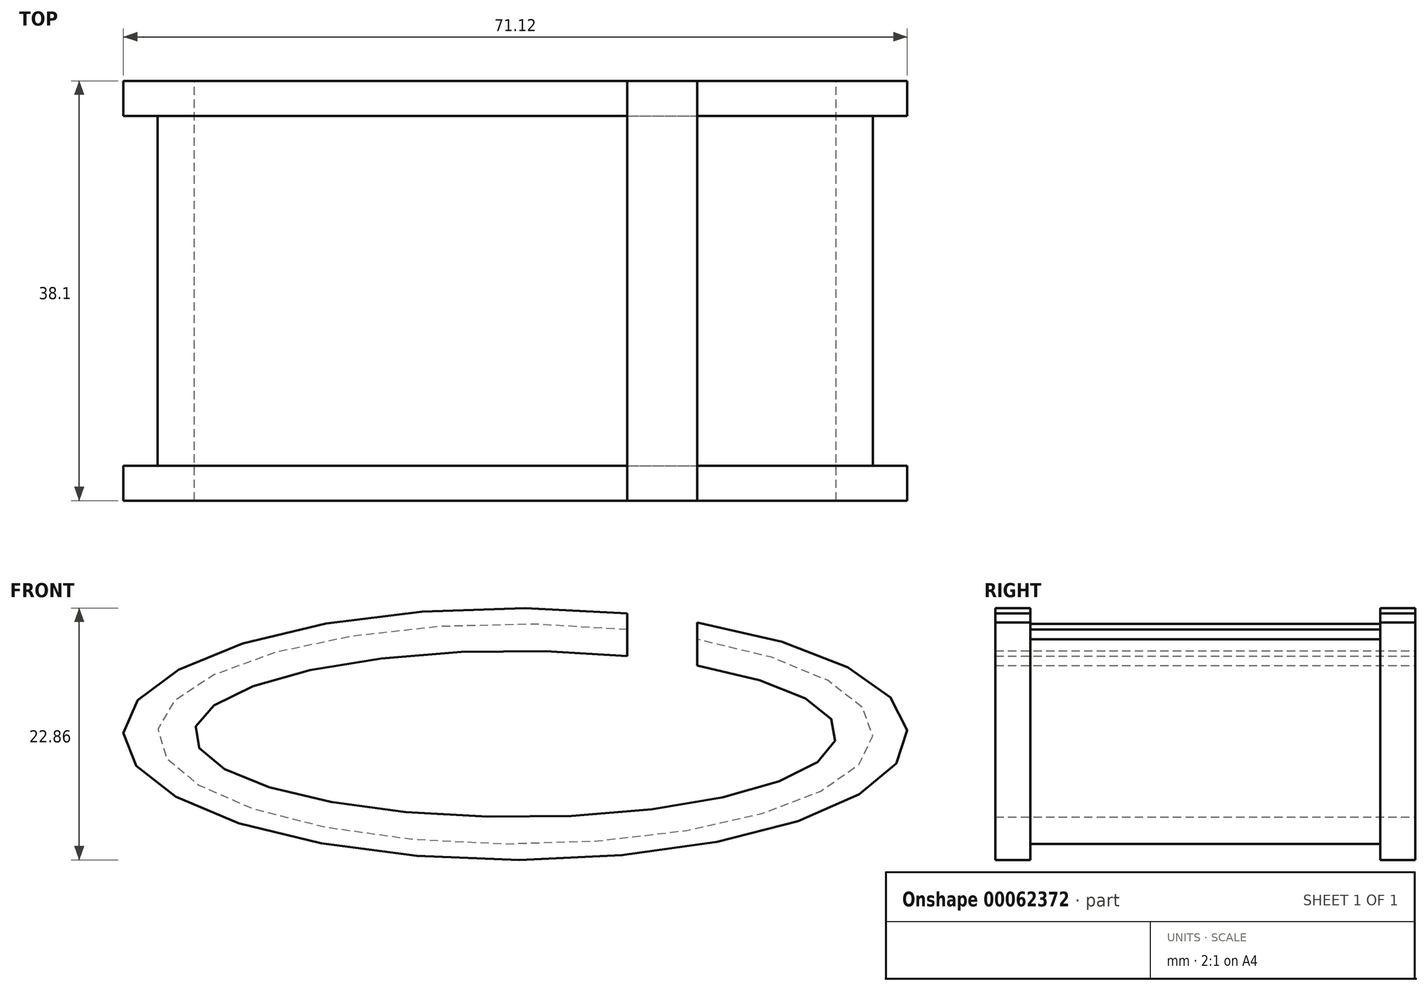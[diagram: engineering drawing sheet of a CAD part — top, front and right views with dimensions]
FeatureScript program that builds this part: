
annotation { "Feature Type Name" : "Feature", "Feature Type Description" : "" }
export const myFeature = defineFeature(function(context is Context, id is Id, definition is map)
    precondition{}
    {
        {
            var Q0;
            Q0=qCreatedBy(makeId("Front.planeOp"),FACE);
            var sketch = newSketch(context, id + "F0", { "sketchPlane" : qUnion([Q0])});
            skLineSegment(sketch, "E0", {"start": v(-32.45, 0) * mm, "end": v(32.45, 0) * mm, "construction": true});
            skLineSegment(sketch, "E1", {"start": v(0, 9.98) * mm, "end": v(0, -9.98) * mm, "construction": true});
            skPoint(sketch, "E2", {"position": v(0, 0) * mm});
            skEllipse(sketch, "E3", {"center": v(0, 0) * mm, "majorRadius": 9.98 * mm, "minorRadius": 32.45 * mm, "majorAxis": v(0, 1)});
            skSolve(sketch);
        }
        {
            var Q0;
            Q0=makeQuery(id+"F0.imprint","IMPRINT",FACE,{"disambiguationData":[TD([[makeQuery(id+"F0.imprint","IMPRINT",EDGE,{"derivedFrom":sQuery(id+"F0.wireOp",EDGE,"E3")}),1.0]])]});
            extrude(context, id + "F1", {"entities" : qUnion([Q0]), "depth" : 15.88 * mm});
        }
        {
            var Q0;
            Q0=makeQuery(id+"F1.opExtrude","CAP_FACE",FACE,{"disambiguationData":[OSD([sQuery(id+"F0.wireOp",EDGE,"E3")])],"isStart":false});
            var sketch = newSketch(context, id + "F2", { "sketchPlane" : qUnion([Q0])});
            skLineSegment(sketch, "E4", {"start": v(0, 0) * mm, "end": v(0, 11.43) * mm, "construction": true});
            skPoint(sketch, "E4.endSnap0", {"position": v(0, 9.98) * mm});
            skLineSegment(sketch, "E5", {"start": v(0, 0) * mm, "end": v(-35.56, 0) * mm, "construction": true});
            skEllipse(sketch, "E6", {"center": v(0, 0) * mm, "majorRadius": 11.43 * mm, "minorRadius": 35.56 * mm, "majorAxis": v(0, 1)});
            skSolve(sketch);
        }
        {
            var Q0;
            Q0 = qSketchRegion(id + "F2", true);
            extrude(context, id + "F3", {"entities" : qUnion([Q0]), "operationType" : NewBodyOperationType.ADD, "depth" : 3.17 * mm});
        }
        {
            var Q0;
            Q0=makeQuery(id+"F1.opExtrude","CAP_FACE",FACE,{"disambiguationData":[OSD([sQuery(id+"F0.wireOp",EDGE,"E3")])],"isStart":true});
            var sketch = newSketch(context, id + "F4", { "sketchPlane" : qUnion([Q0])});
            skLineSegment(sketch, "E7", {"start": v(0, 0) * mm, "end": v(0, 7.55) * mm, "construction": true});
            skLineSegment(sketch, "E8", {"start": v(0, 0) * mm, "end": v(-29.12, 0) * mm, "construction": true});
            skEllipse(sketch, "E9", {"center": v(0, 0) * mm, "majorRadius": 7.55 * mm, "minorRadius": 29.12 * mm, "majorAxis": v(0, 1)});
            skSolve(sketch);
        }
        {
            var Q0;
            Q0 = qSketchRegion(id + "F4", true);
            extrude(context, id + "F5", {"entities" : qUnion([Q0]), "operationType" : NewBodyOperationType.REMOVE, "endBound" : BoundingType.THROUGH_ALL, "oppositeDirection" : true, "depth" : 25.4 * mm});
        }
        {
            var Q0;
            Q0=makeQuery(id+"F3.opExtrude","CAP_FACE",FACE,{"disambiguationData":[OSD([sQuery(id+"F2.wireOp",EDGE,"E6")])],"isStart":false});
            var sketch = newSketch(context, id + "F6", { "sketchPlane" : qUnion([Q0])});
            skLineSegment(sketch, "E10.bottom", {"start": v(10.16, 12.19) * mm, "end": v(16.51, 12.19) * mm});
            skLineSegment(sketch, "E10.top", {"start": v(10.16, 4) * mm, "end": v(16.51, 4) * mm});
            skLineSegment(sketch, "E10.left", {"start": v(10.16, 12.19) * mm, "end": v(10.16, 4) * mm});
            skLineSegment(sketch, "E10.right", {"start": v(16.51, 12.19) * mm, "end": v(16.51, 4) * mm});
            skSolve(sketch);
        }
        {
            var Q0;
            Q0 = qSketchRegion(id + "F6", true);
            extrude(context, id + "F7", {"entities" : qUnion([Q0]), "operationType" : NewBodyOperationType.REMOVE, "endBound" : BoundingType.THROUGH_ALL, "oppositeDirection" : true, "depth" : 25.4 * mm});
        }
        {
            var Q0;
            Q0=makeQuery(id+"F1.opExtrude","SWEPT_BODY",BODY,{"disambiguationData":[OSD([sQuery(id+"F0.wireOp",EDGE,"E3")])]});
            var Q1;
            Q1=makeQuery(id+"F1.opExtrude","CAP_FACE",FACE,{"disambiguationData":[OSD([sQuery(id+"F0.wireOp",EDGE,"E3")])],"isStart":true});
            mirror(context, id + "F8", {"operationType" : NewBodyOperationType.ADD, "entities" : qUnion([Q0]), "mirrorPlane" : qUnion([Q1])});
        }
    });
